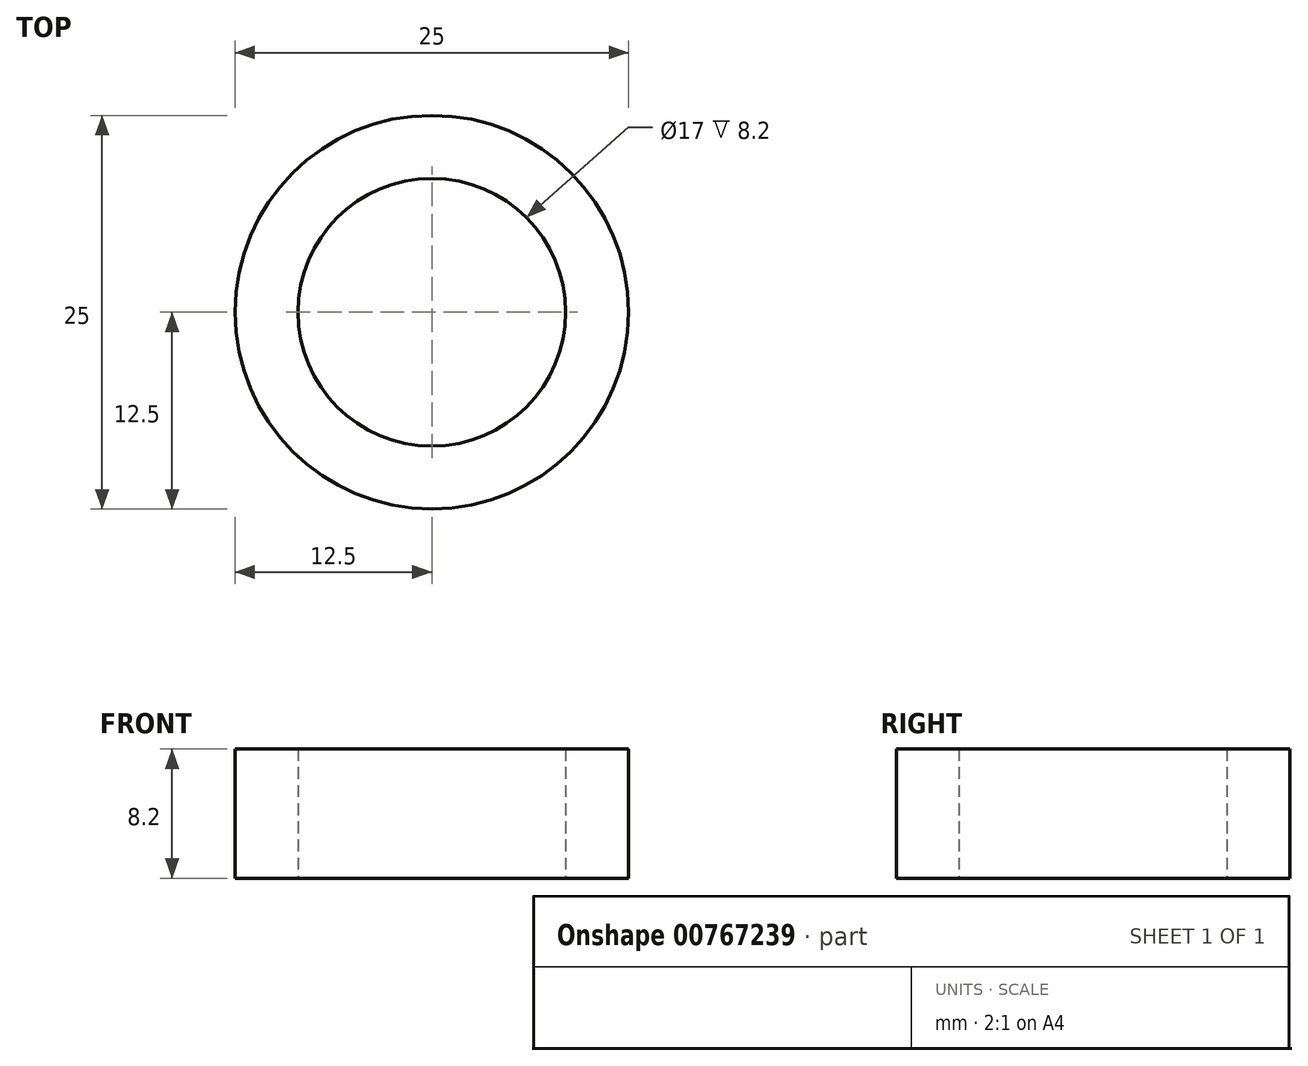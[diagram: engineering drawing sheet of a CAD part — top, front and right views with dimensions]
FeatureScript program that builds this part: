
annotation { "Feature Type Name" : "Feature", "Feature Type Description" : "" }
export const myFeature = defineFeature(function(context is Context, id is Id, definition is map)
    precondition{}
    {
        {
            var Q0;
            Q0=qCreatedBy(makeId("Top.planeOp"),FACE);
            var sketch = newSketch(context, id + "F0", { "sketchPlane" : qUnion([Q0])});
            skCircle(sketch, "E0", {"center": v(0, 0) * mm, "radius": 8.5 * mm});
            skCircle(sketch, "E1", {"center": v(0, 0) * mm, "radius": 12.5 * mm});
            skSolve(sketch);
        }
        {
            var Q0;
            Q0=makeQuery(id+"F0.imprint","IMPRINT",FACE,{"disambiguationData":[TD([[makeQuery(id+"F0.imprint","IMPRINT",EDGE,{"derivedFrom":sQuery(id+"F0.wireOp",EDGE,"E0")}),-1.0]])]});
            extrude(context, id + "F1", {"entities" : qUnion([Q0]), "depth" : 8.2 * mm, "offsetDistance" : 25 * mm});
        }
    });
